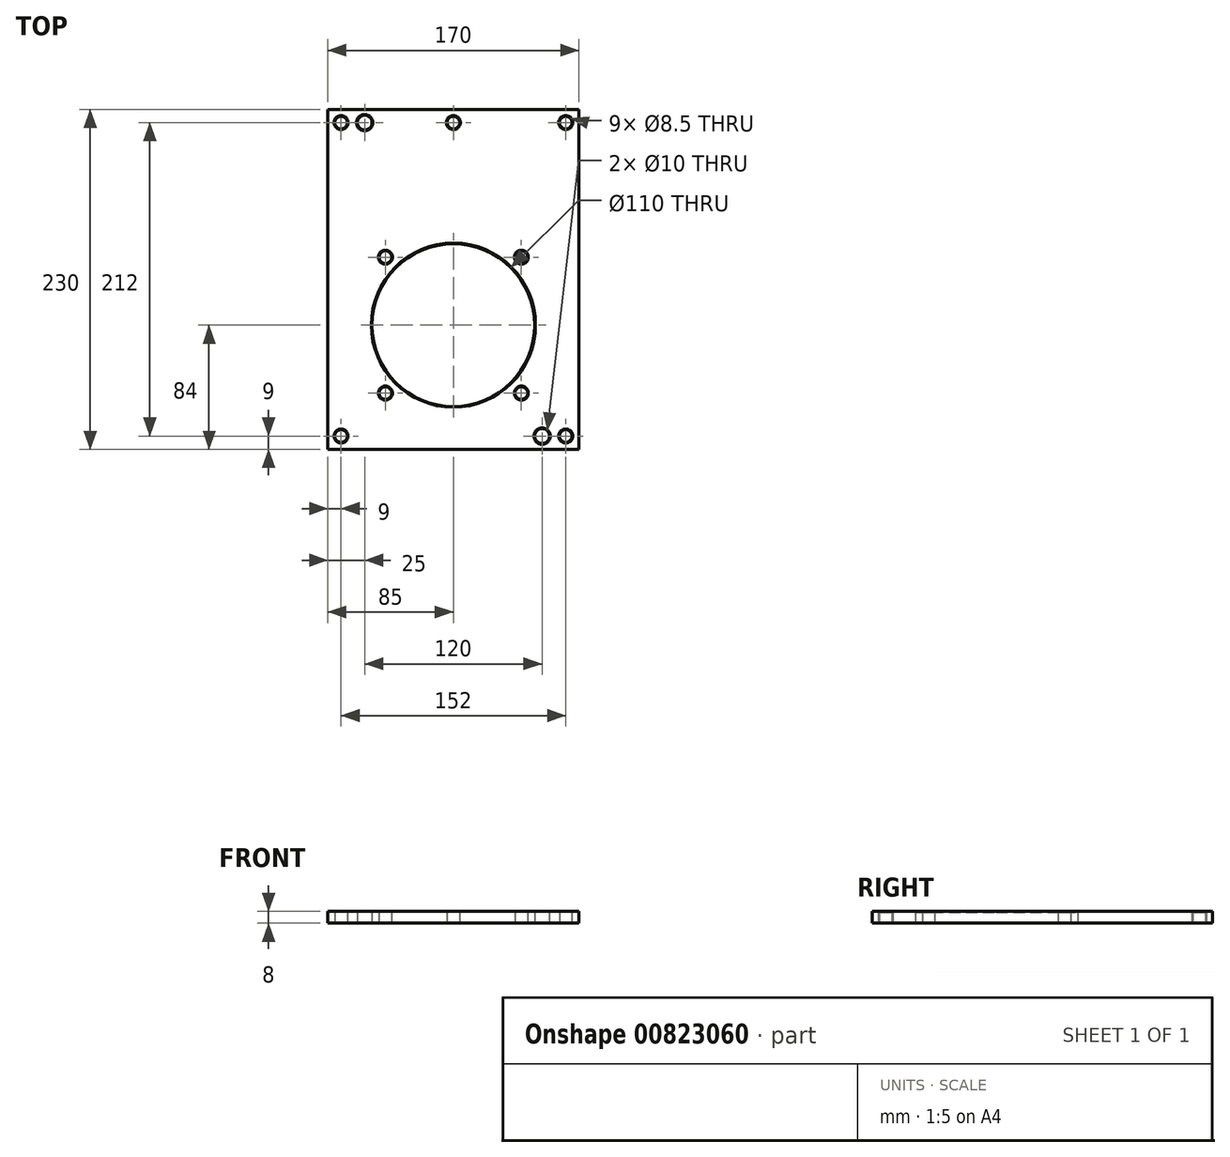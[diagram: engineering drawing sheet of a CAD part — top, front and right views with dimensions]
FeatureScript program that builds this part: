
annotation { "Feature Type Name" : "Feature", "Feature Type Description" : "" }
export const myFeature = defineFeature(function(context is Context, id is Id, definition is map)
    precondition{}
    {
        {
            var Q0;
            Q0=qCreatedBy(makeId("Top.planeOp"),FACE);
            var sketch = newSketch(context, id + "F0", { "sketchPlane" : qUnion([Q0])});
            skCircle(sketch, "E0", {"center": v(0, 0) * mm, "radius": 55 * mm});
            skLineSegment(sketch, "E1", {"start": v(0, 0) * mm, "end": v(152.93, 0) * mm, "construction": true});
            skLineSegment(sketch, "E2", {"start": v(0, 194.5) * mm, "end": v(0, 0) * mm, "construction": true});
            skCircle(sketch, "E3", {"center": v(0, 0) * mm, "radius": 65 * mm, "construction": true});
            skLineSegment(sketch, "E4", {"start": v(0, 0) * mm, "end": v(45.96, 45.96) * mm, "construction": true});
            skCircle(sketch, "E5", {"center": v(45.96, 45.96) * mm, "radius": 4.25 * mm});
            skCircle(sketch, "E6.1.0", {"center": v(-45.96, 45.96) * mm, "radius": 4.25 * mm});
            skCircle(sketch, "E6.2.0", {"center": v(-45.96, -45.96) * mm, "radius": 4.25 * mm});
            skCircle(sketch, "E6.3.0", {"center": v(45.96, -45.96) * mm, "radius": 4.25 * mm});
            skLineSegment(sketch, "E7.bottom", {"start": v(85, -84) * mm, "end": v(-85, -84) * mm});
            skLineSegment(sketch, "E7.top", {"start": v(85, 146) * mm, "end": v(-85, 146) * mm});
            skLineSegment(sketch, "E7.left", {"start": v(85, -84) * mm, "end": v(85, 146) * mm});
            skLineSegment(sketch, "E7.right", {"start": v(-85, -84) * mm, "end": v(-85, 146) * mm});
            skPoint(sketch, "E7.middle", {"position": v(0, 31) * mm});
            skCircle(sketch, "E8", {"center": v(0, 0) * mm, "radius": 80 * mm, "construction": true});
            skLineSegment(sketch, "E9.0", {"start": v(85, -66) * mm, "end": v(-85, -66) * mm, "construction": true});
            skLineSegment(sketch, "E10.0", {"start": v(85, 128) * mm, "end": v(-85, 128) * mm, "construction": true});
            skLineSegment(sketch, "E11", {"start": v(-85, 137) * mm, "end": v(85, 137) * mm, "construction": true});
            skLineSegment(sketch, "E12", {"start": v(-85, -75) * mm, "end": v(85, -75) * mm, "construction": true});
            skLineSegment(sketch, "E13.0", {"start": v(-76, -84) * mm, "end": v(-76, 146) * mm, "construction": true});
            skLineSegment(sketch, "E14.0", {"start": v(76, -84) * mm, "end": v(76, 146) * mm, "construction": true});
            skCircle(sketch, "E15", {"center": v(-76, 137) * mm, "radius": 4.25 * mm});
            skCircle(sketch, "E16", {"center": v(76, 137) * mm, "radius": 4.25 * mm});
            skCircle(sketch, "E17", {"center": v(76, -75) * mm, "radius": 4.25 * mm});
            skCircle(sketch, "E18", {"center": v(-76, -75) * mm, "radius": 4.25 * mm});
            skCircle(sketch, "E19", {"center": v(60, -75) * mm, "radius": 5 * mm});
            skCircle(sketch, "E20", {"center": v(-60, 137) * mm, "radius": 5 * mm});
            skCircle(sketch, "E21", {"center": v(0, 137) * mm, "radius": 4.25 * mm});
            skSolve(sketch);
        }
        {
            var Q0;
            Q0 = qSketchRegion(id + "F0", true);
            extrude(context, id + "F1", {"entities" : qUnion([Q0]), "depth" : 8 * mm, "offsetDistance" : 25 * mm});
        }
        {
            var Q0;
            Q0=makeQuery(id+"F1.opExtrude","SWEPT_FACE",FACE,{"disambiguationData":[OSD([sQuery(id+"F0.wireOp",EDGE,"E18")])]});
            var Q1;
            Q1=makeQuery(id+"F1.opExtrude","SWEPT_FACE",FACE,{"disambiguationData":[OSD([sQuery(id+"F0.wireOp",EDGE,"E6.2.0")])]});
            var Q2;
            Q2=makeQuery(id+"F1.opExtrude","SWEPT_FACE",FACE,{"disambiguationData":[OSD([sQuery(id+"F0.wireOp",EDGE,"E19")])]});
            var Q3;
            Q3=makeQuery(id+"F1.opExtrude","SWEPT_FACE",FACE,{"disambiguationData":[OSD([sQuery(id+"F0.wireOp",EDGE,"E6.3.0")])]});
            var Q4;
            Q4=makeQuery(id+"F1.opExtrude","SWEPT_FACE",FACE,{"disambiguationData":[OSD([sQuery(id+"F0.wireOp",EDGE,"E5")])]});
            var Q5;
            Q5=makeQuery(id+"F1.opExtrude","SWEPT_FACE",FACE,{"disambiguationData":[OSD([sQuery(id+"F0.wireOp",EDGE,"E6.1.0")])]});
            var Q6;
            Q6=makeQuery(id+"F1.opExtrude","SWEPT_FACE",FACE,{"disambiguationData":[OSD([sQuery(id+"F0.wireOp",EDGE,"E0")])]});
            var Q7;
            Q7=makeQuery(id+"F1.opExtrude","SWEPT_FACE",FACE,{"disambiguationData":[OSD([sQuery(id+"F0.wireOp",EDGE,"E17")])]});
            var Q8;
            Q8=makeQuery(id+"F1.opExtrude","SWEPT_FACE",FACE,{"disambiguationData":[OSD([sQuery(id+"F0.wireOp",EDGE,"E16")])]});
            var Q9;
            Q9=makeQuery(id+"F1.opExtrude","SWEPT_FACE",FACE,{"disambiguationData":[OSD([sQuery(id+"F0.wireOp",EDGE,"E20")])]});
            var Q10;
            Q10=makeQuery(id+"F1.opExtrude","SWEPT_FACE",FACE,{"disambiguationData":[OSD([sQuery(id+"F0.wireOp",EDGE,"E15")])]});
            var Q11;
            Q11=makeQuery(id+"F1.opExtrude","SWEPT_FACE",FACE,{"disambiguationData":[OSD([sQuery(id+"F0.wireOp",EDGE,"E21")])]});
            chamfer(context, id + "F2", {"entities" : qUnion([Q0, Q1, Q2, Q3, Q4, Q5, Q6, Q7, Q8, Q9, Q10, Q11]), "width" : 0.5 * mm, "tangentPropagation" : true});
        }
    });
